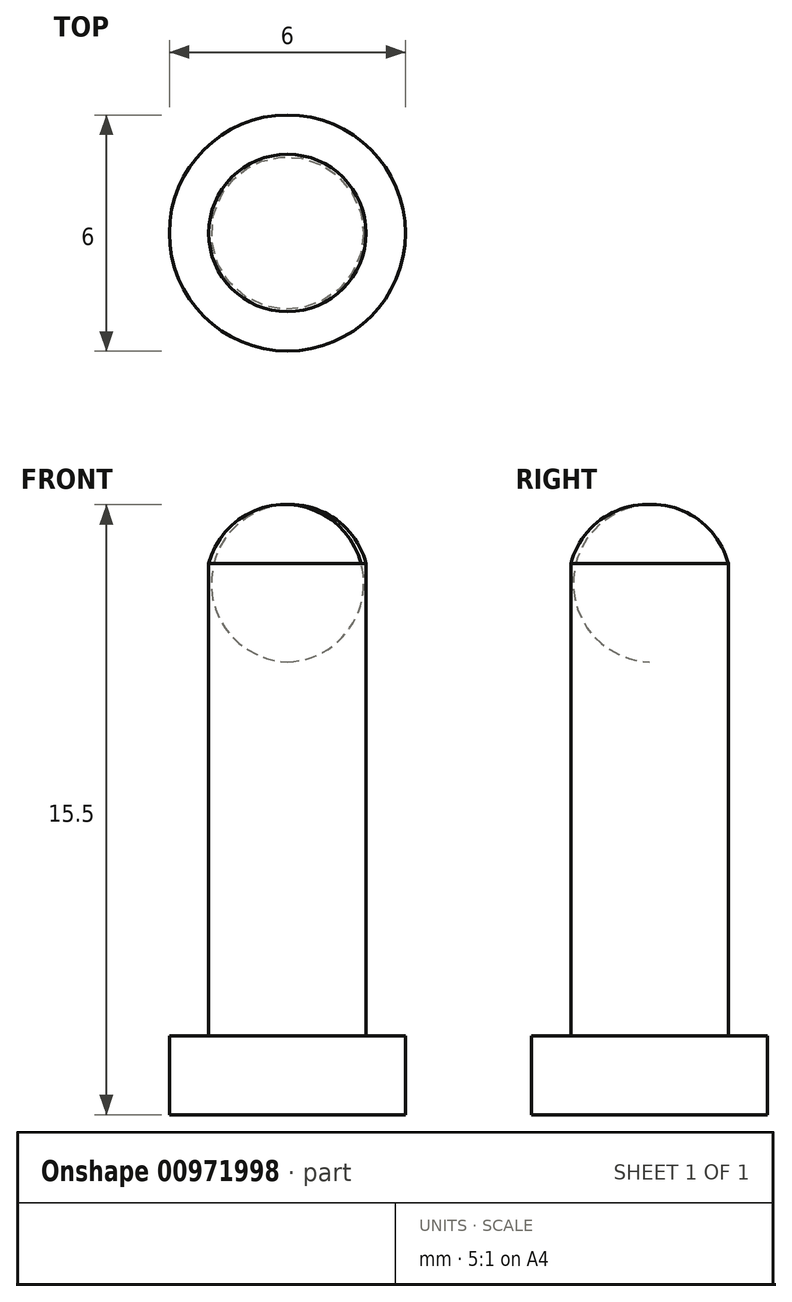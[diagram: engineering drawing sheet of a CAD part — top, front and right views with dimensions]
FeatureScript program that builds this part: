
annotation { "Feature Type Name" : "Feature", "Feature Type Description" : "" }
export const myFeature = defineFeature(function(context is Context, id is Id, definition is map)
    precondition{}
    {
        {
            var Q0;
            Q0=qCreatedBy(makeId("Front.planeOp"),FACE);
            var sketch = newSketch(context, id + "F0", { "sketchPlane" : qUnion([Q0])});
            skLineSegment(sketch, "E0.bottom", {"start": v(1.5, -1) * mm, "end": v(-1.5, -1) * mm});
            skLineSegment(sketch, "E0.top", {"start": v(1.5, 1) * mm, "end": v(-1.5, 1) * mm});
            skLineSegment(sketch, "E0.left", {"start": v(1.5, -1) * mm, "end": v(1.5, 1) * mm});
            skLineSegment(sketch, "E0.right", {"start": v(-1.5, -1) * mm, "end": v(-1.5, 1) * mm});
            skPoint(sketch, "E0.middle", {"position": v(0, 0) * mm});
            skLineSegment(sketch, "E1.bottom", {"start": v(-1.5, 1) * mm, "end": v(0.5, 1) * mm});
            skLineSegment(sketch, "E1.top", {"start": v(-1.5, 13) * mm, "end": v(0.5, 13) * mm});
            skLineSegment(sketch, "E1.left", {"start": v(-1.5, 1) * mm, "end": v(-1.5, 13) * mm});
            skLineSegment(sketch, "E1.right", {"start": v(0.5, 1) * mm, "end": v(0.5, 13) * mm});
            skLineSegment(sketch, "E2", {"start": v(-1.5, 13) * mm, "end": v(-1.5, 14.5) * mm});
            skArc(sketch, "E3", {"start": v(0.5, 13) * mm, "mid": v(-0.24, 14.1) * mm, "end": v(-1.5, 14.5) * mm});
            skSolve(sketch);
        }
        {
            var Q0;
            Q0=makeQuery(id+"F0.imprint","IMPRINT",FACE,{"disambiguationData":[TD([[makeQuery(id+"F0.imprint","IMPRINT",EDGE,{"derivedFrom":sQuery(id+"F0.wireOp",EDGE,"E1.top")}),1.0]])]});
            var Q1;
            Q1=makeQuery(id+"F0.imprint","IMPRINT",FACE,{"disambiguationData":[TD([[makeQuery(id+"F0.imprint","IMPRINT",EDGE,{"derivedFrom":sQuery(id+"F0.wireOp",EDGE,"E1.top")}),-1.0]])]});
            var Q2;
            Q2=makeQuery(id+"F0.imprint","IMPRINT",FACE,{"disambiguationData":[TD([[makeQuery(id+"F0.imprint","IMPRINT",EDGE,{"derivedFrom":sQuery(id+"F0.wireOp",EDGE,"E0.bottom")}),-1.0]])]});
            var Q3;
            Q3=sQuery(id+"F0.wireOp",EDGE,"E1.left");
            revolve(context, id + "F1", {"surfaceOperationType" : NewSurfaceOperationType.NEW, "entities" : qUnion([Q0, Q1, Q2]), "axis" : qUnion([Q3]), "revolveType" : RevolveType.FULL});
        }
    });
